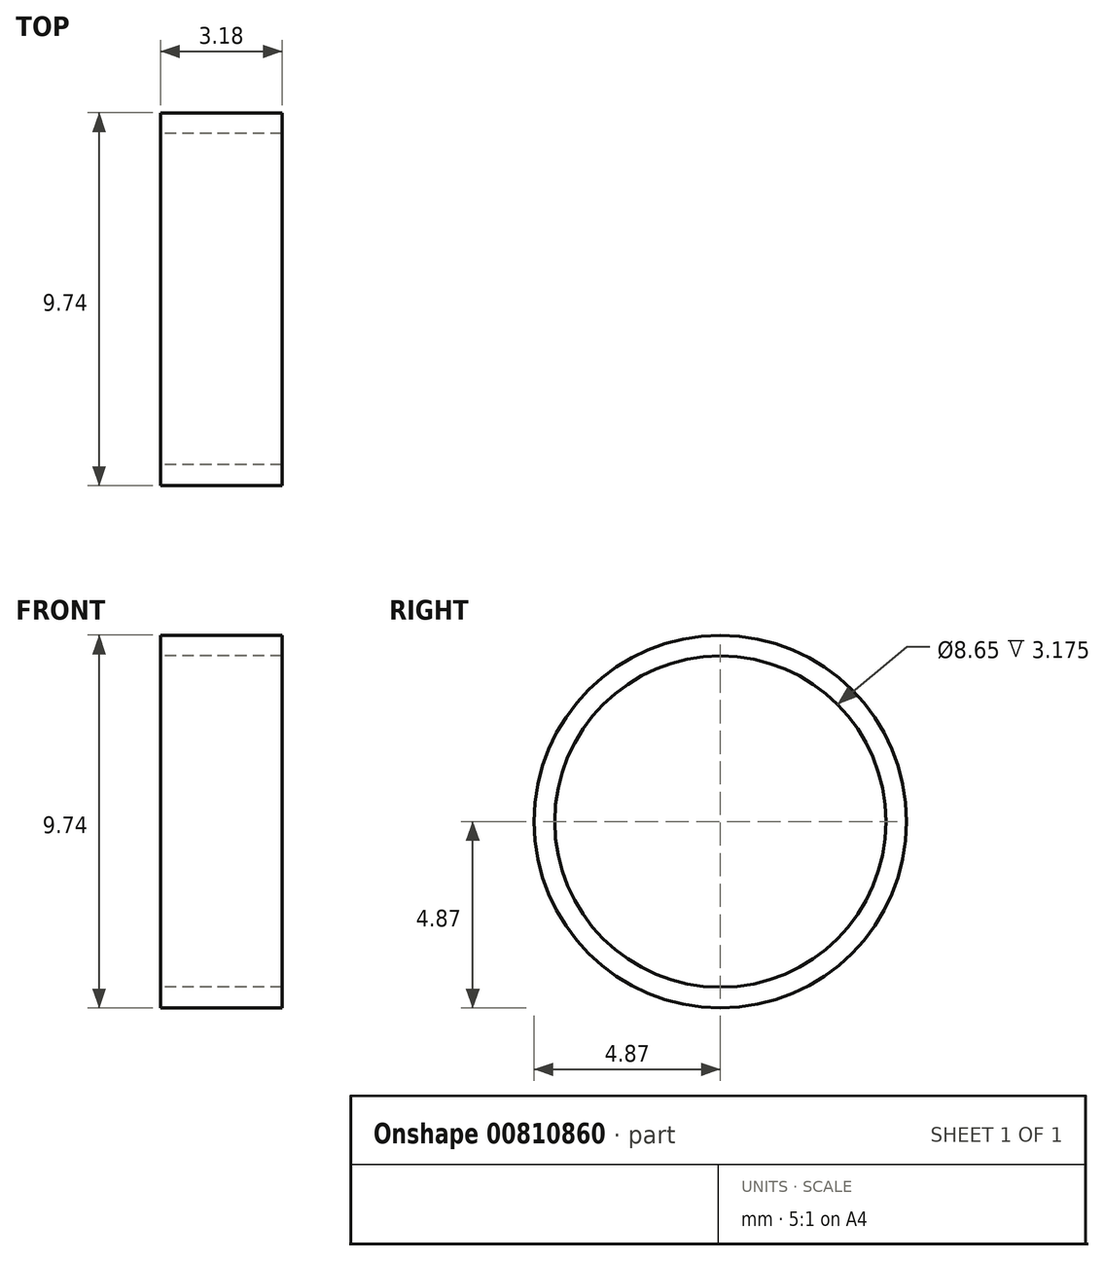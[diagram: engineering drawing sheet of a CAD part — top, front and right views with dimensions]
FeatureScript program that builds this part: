
annotation { "Feature Type Name" : "Feature", "Feature Type Description" : "" }
export const myFeature = defineFeature(function(context is Context, id is Id, definition is map)
    precondition{}
    {
        {
            var Q0;
            Q0=qCreatedBy(makeId("Right.planeOp"),FACE);
            var sketch = newSketch(context, id + "F0", { "sketchPlane" : qUnion([Q0])});
            skCircle(sketch, "E0", {"center": v(0, 0) * mm, "radius": 4.87 * mm});
            skCircle(sketch, "E1", {"center": v(0, 0) * mm, "radius": 4.32 * mm});
            skSolve(sketch);
        }
        {
            var Q0;
            Q0=makeQuery(id+"F0.imprint","IMPRINT",FACE,{"disambiguationData":[TD([[makeQuery(id+"F0.imprint","IMPRINT",EDGE,{"derivedFrom":sQuery(id+"F0.wireOp",EDGE,"E0")}),1.0]])]});
            extrude(context, id + "F1", {"entities" : qUnion([Q0]), "depth" : 3.17 * mm, "offsetDistance" : 25.4 * mm});
        }
    });
